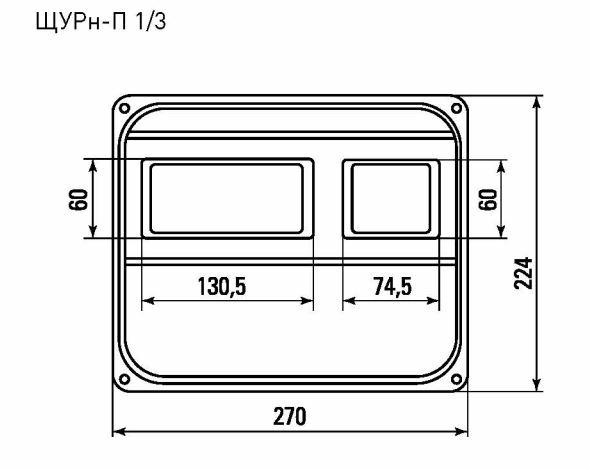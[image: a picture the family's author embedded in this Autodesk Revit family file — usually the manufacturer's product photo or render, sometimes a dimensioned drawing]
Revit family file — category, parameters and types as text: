
# Revit family: EKF_EE_Короб_КЭТ_Силовой(1200х300х150)_Basic
name_source: partatom
category: Электрооборудование
units: mm (PartAtom-declared; Revit-internal decimal feet)

## family parameters
Всегда вертикально = Да
На основе рабочей плоскости = Нет
Общий = Нет
При загрузке вырезать с полостями = Нет
Размер круглого соединителя = Использовать диаметр
Тип детали = Силовой щит
Точка расчета площади = Да

## types (1)
- Короб КЭТ силовой (1200х300х150) EKF Basic
    ADSK_Единица измерения = компл.
    ADSK_Завод-изготовитель = EKF
    ADSK_Классификация нагрузок = Прочее
    ADSK_Код изделия = uerm2-ket-s-1200-bas
    ADSK_Количество = 1
    ADSK_Количество фаз = 3
    ADSK_Коэффициент мощности = 1
    ADSK_Марка = Короб КЭТ силовой
    ADSK_Масса = 0
    ADSK_Материал = RAL 7035_Сталь
    ADSK_Наименование = Короб КЭТ силовой (1200х300х150) EKF BasicКороб КЭТ силовой (1200х300х150) EKF Basic
    ADSK_Напряжение = 400 В
    ADSK_Номинальная мощность = 0 Вт
    ADSK_Обозначение = Короб КЭТ силовой
    ADSK_Полная мощность = 0 В·А
    ADSK_Размер_Высота = 1200 мм
    ADSK_Размер_Глубина = 150 мм
    ADSK_Размер_Ширина = 300 мм
    ADSK_Ток = 125 А
    Изготовитель = EKF
    Количество DIN-реек = 0
    Количество модулей на DIN-рейке = 0
    Максимальное количество модулей = 0
    Описание = Короб КЭТ силовой (1200х300х150) EKF BasicКороб КЭТ силовой (1200х300х150) EKF Basic
    Серия номенклатуры = Basic
    Степень защиты IP = IP31
    ТВ = EKF
    Тип = 211 мм
    Тип установки = Навесной
